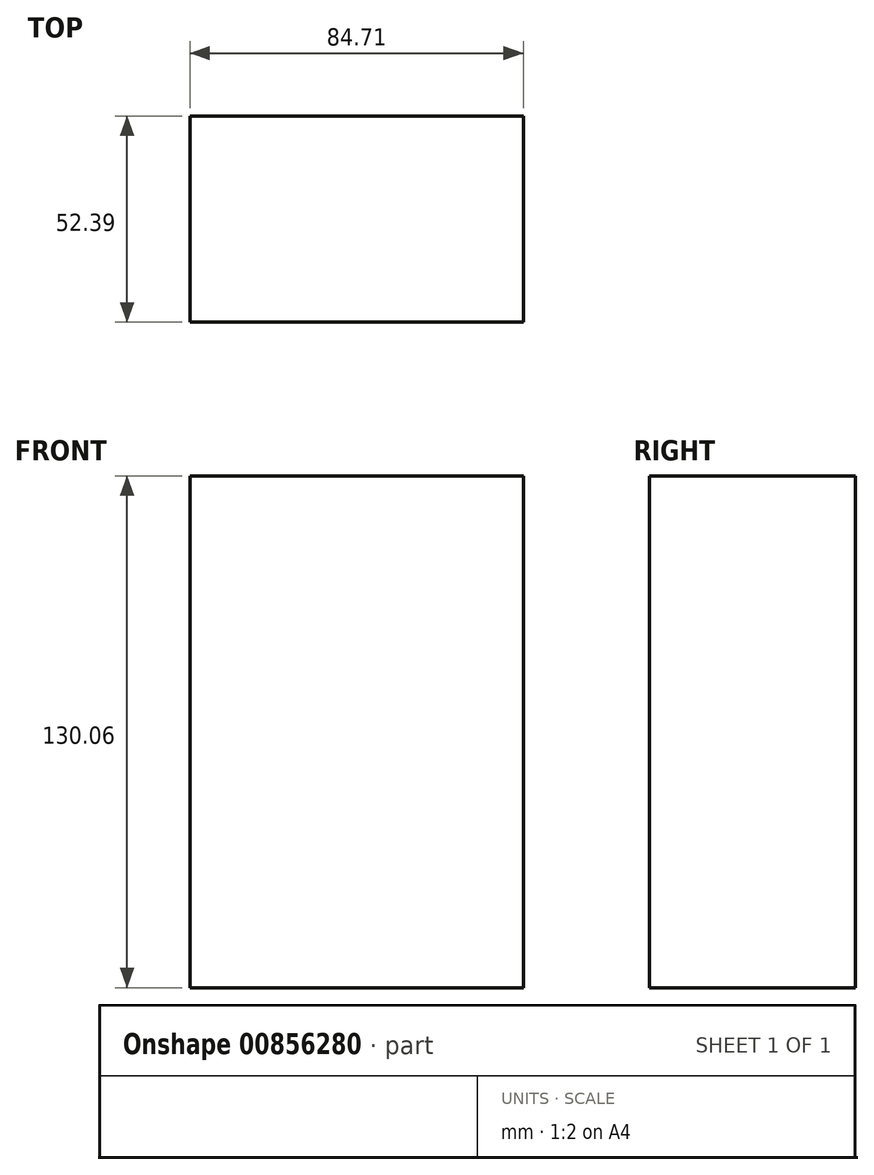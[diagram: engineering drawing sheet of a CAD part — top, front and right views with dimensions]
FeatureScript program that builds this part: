
annotation { "Feature Type Name" : "Feature", "Feature Type Description" : "" }
export const myFeature = defineFeature(function(context is Context, id is Id, definition is map)
    precondition{}
    {
        {
            var Q0;
            Q0=qCreatedBy(makeId("Top.planeOp"),FACE);
            var sketch = newSketch(context, id + "F0", { "sketchPlane" : qUnion([Q0])});
            skLineSegment(sketch, "E0.bottom", {"start": v(-34.29, -16.76) * mm, "end": v(50.42, -16.76) * mm});
            skLineSegment(sketch, "E0.top", {"start": v(-34.29, 35.63) * mm, "end": v(50.42, 35.63) * mm});
            skLineSegment(sketch, "E0.left", {"start": v(-34.29, -16.76) * mm, "end": v(-34.29, 35.63) * mm});
            skLineSegment(sketch, "E0.right", {"start": v(50.42, -16.76) * mm, "end": v(50.42, 35.63) * mm});
            skSolve(sketch);
        }
        {
            var Q0;
            Q0=makeQuery(id+"F0.imprint","IMPRINT",FACE,{"disambiguationData":[TD([[makeQuery(id+"F0.imprint","IMPRINT",EDGE,{"derivedFrom":sQuery(id+"F0.wireOp",EDGE,"E0.bottom")}),1.0]])]});
            extrude(context, id + "F1", {"entities" : qUnion([Q0]), "depth" : 130.06 * mm, "offsetDistance" : 25.4 * mm});
        }
    });
